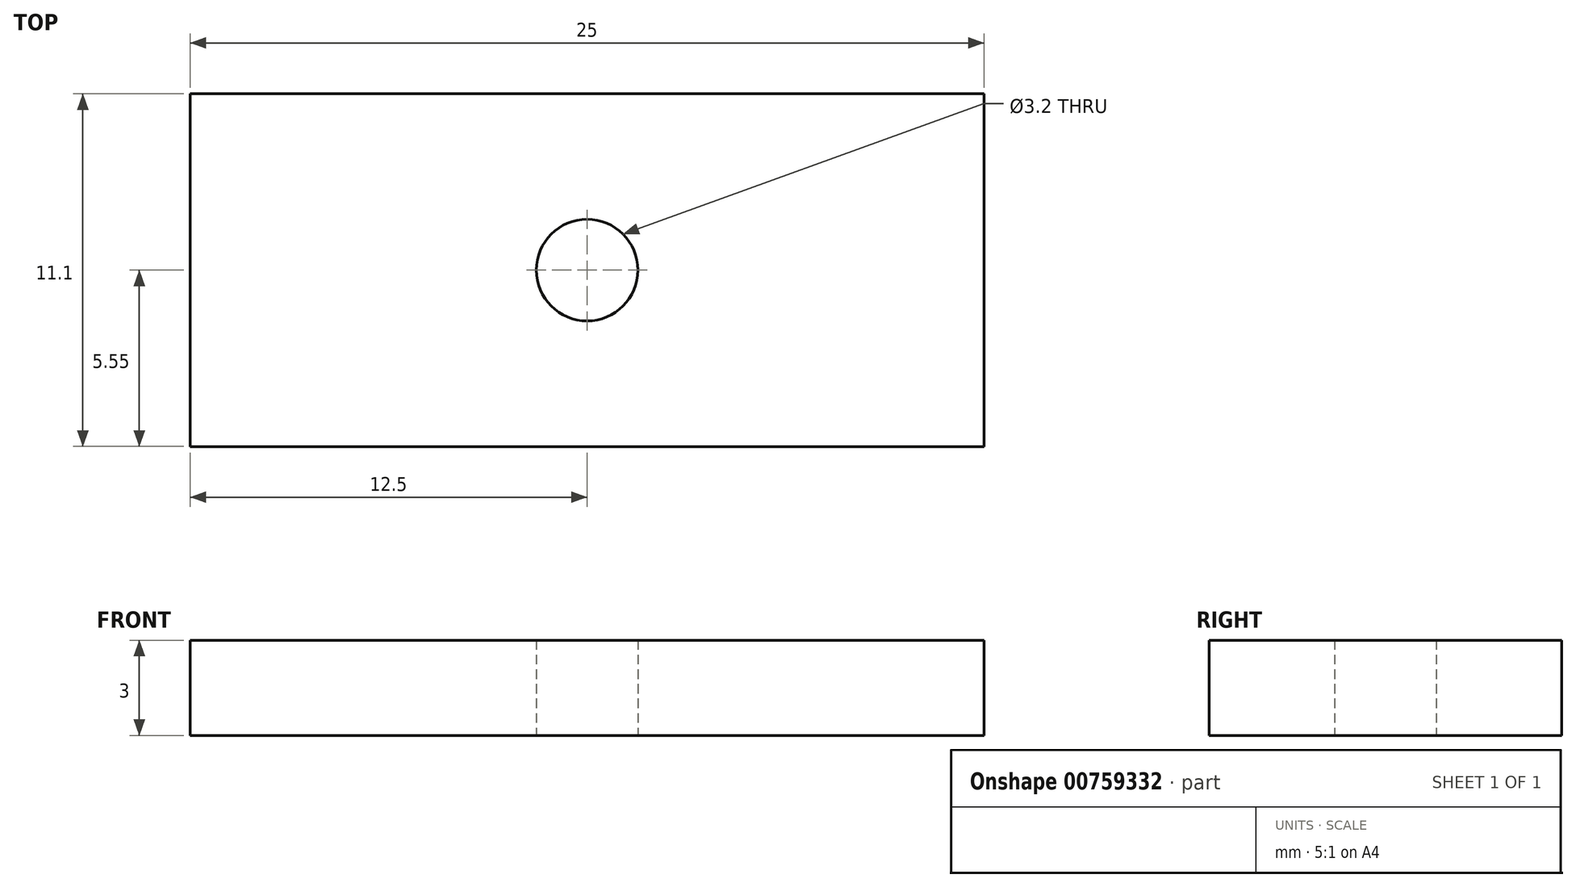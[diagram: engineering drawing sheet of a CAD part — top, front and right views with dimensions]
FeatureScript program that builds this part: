
annotation { "Feature Type Name" : "Feature", "Feature Type Description" : "" }
export const myFeature = defineFeature(function(context is Context, id is Id, definition is map)
    precondition{}
    {
        {
            var Q0;
            Q0=qCreatedBy(makeId("Top.planeOp"),FACE);
            var sketch = newSketch(context, id + "F0", { "sketchPlane" : qUnion([Q0])});
            skLineSegment(sketch, "E0.bottom", {"start": v(-12.5, 5.56) * mm, "end": v(12.5, 5.56) * mm});
            skLineSegment(sketch, "E0.top", {"start": v(-12.5, -5.55) * mm, "end": v(12.5, -5.55) * mm});
            skLineSegment(sketch, "E0.left", {"start": v(-12.5, 5.56) * mm, "end": v(-12.5, -5.55) * mm});
            skLineSegment(sketch, "E0.right", {"start": v(12.5, 5.56) * mm, "end": v(12.5, -5.55) * mm});
            skPoint(sketch, "E0.middle", {"position": v(0, 0) * mm});
            skCircle(sketch, "E1", {"center": v(0, 0) * mm, "radius": 1.6 * mm});
            skSolve(sketch);
        }
        {
            var Q0;
            Q0 = qSketchRegion(id + "F0", true);
            extrude(context, id + "F1", {"entities" : qUnion([Q0]), "depth" : 3 * mm, "offsetDistance" : 25 * mm});
        }
    });
